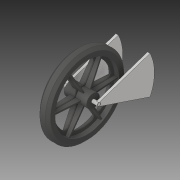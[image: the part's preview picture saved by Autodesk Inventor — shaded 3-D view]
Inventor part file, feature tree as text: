
AUTODESK INVENTOR PART (.ipt)
format: ipt  version: 2017 (Build 210142000, 142)  size: 318,464 bytes
history: native  units: mm
features: other x3, extrude x3, sketch x3, thicken_offset x2, plane x1, mirror x1
ambient origin geometry x8: Origin, YZ Plane, XZ Plane, XY Plane, X Axis, Y Axis, Z Axis, Center Point
bodies: Solid1 (feature_tree)
feature tree (13):
  other  "wheel.ipt"
  extrude  "Extrusion1"  Depth=7.0mm TaperAngle=0.0deg
  extrude  "Extrusion2"  Depth=3.0mm TaperAngle=0.0deg
  extrude  "Extrusion3"  Depth=30.0mm
  plane  "Work Plane1"
  mirror  "Mirror1"
  thicken_offset  "Thicken1"
  thicken_offset  "Thicken2"
  other  "Solid19::wheel.ipt"
  other  "TaggingFeature1"
  sketch  "Sketch1"  dims[d0=5.0mm d1=7.0mm d2=0.0mm]
  sketch  "Sketch2"  dims[d3=7.0mm d4=0.0mm d5=3.0mm d6=0.0mm]
  sketch  "Sketch3"  dims[d7=-20.3mm d8=30.0mm d9=30.0mm d10=30.0mm d11=30.0mm]
